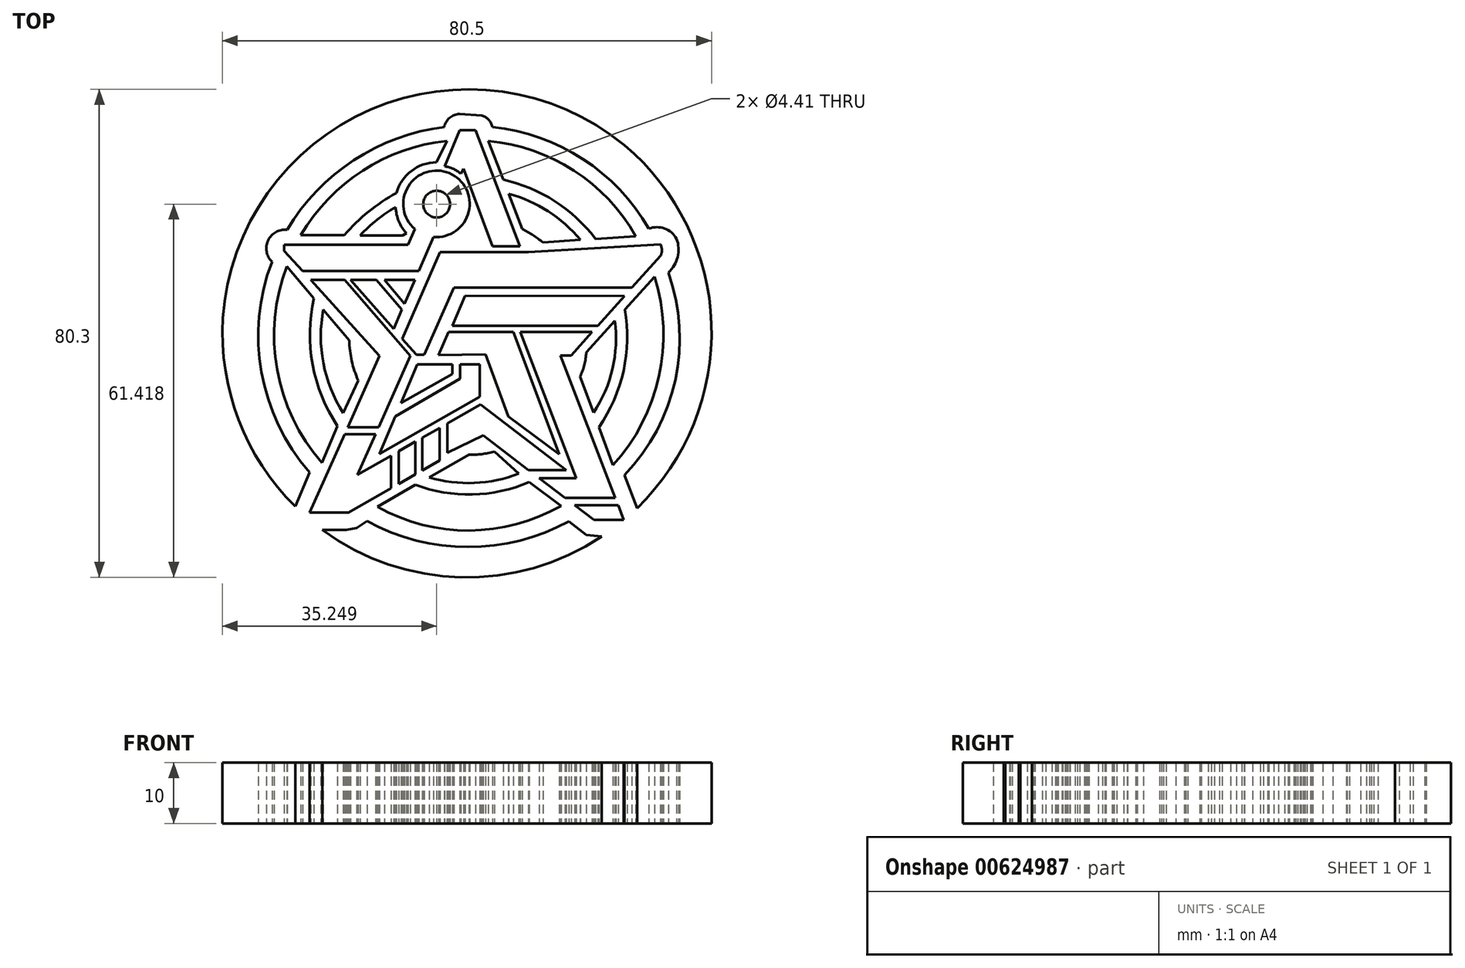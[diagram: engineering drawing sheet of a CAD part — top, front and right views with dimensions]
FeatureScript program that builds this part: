
annotation { "Feature Type Name" : "Feature", "Feature Type Description" : "" }
export const myFeature = defineFeature(function(context is Context, id is Id, definition is map)
    precondition{}
    {
        {
            var Q0;
            Q0=qCreatedBy(makeId("Top.planeOp"),FACE);
            var sketch = newSketch(context, id + "F0", { "sketchPlane" : qUnion([Q0])});
            skCircle(sketch, "E0", {"center": v(0, 0) * mm, "radius": 19.62 * mm, "construction": true});
            skCircle(sketch, "E1", {"center": v(0, 0) * mm, "radius": 24.24 * mm, "construction": true});
            skCircle(sketch, "E2", {"center": v(0, 0) * mm, "radius": 34.5 * mm, "construction": true});
            skLineSegment(sketch, "E3", {"start": v(20.7, -30.4) * mm, "end": v(2.49, -16.49) * mm, "construction": true});
            skLineSegment(sketch, "E4", {"start": v(2.49, -16.49) * mm, "end": v(-19.72, -29.2) * mm, "construction": true});
            skLineSegment(sketch, "E5", {"start": v(2, -11.38) * mm, "end": v(-18.24, -22.97) * mm, "construction": true});
            skLineSegment(sketch, "E6", {"start": v(-18.24, -22.97) * mm, "end": v(-9.56, -3.39) * mm, "construction": true});
            skLineSegment(sketch, "E7", {"start": v(-5.7, 16.2) * mm, "end": v(-12.28, 1.1) * mm, "construction": true});
            skLineSegment(sketch, "E8", {"start": v(-25.9, 9.11) * mm, "end": v(-8.79, 9.11) * mm, "construction": true});
            skLineSegment(sketch, "E9", {"start": v(23.83, -21.37) * mm, "end": v(18.4, -6.8) * mm, "construction": true});
            skLineSegment(sketch, "E10", {"start": v(30.66, 9.62) * mm, "end": v(19.42, -2.8) * mm, "construction": true});
            skLineSegment(sketch, "E11", {"start": v(25.58, -30.36) * mm, "end": v(15.19, -3.34) * mm, "construction": true});
            skLineSegment(sketch, "E12", {"start": v(15.19, -3.34) * mm, "end": v(16.91, -3.34) * mm, "construction": true});
            skLineSegment(sketch, "E13", {"start": v(16.91, -3.34) * mm, "end": v(31.66, 13.12) * mm, "construction": true});
            skLineSegment(sketch, "E14", {"start": v(27.56, 16.32) * mm, "end": v(12.3, 15.29) * mm, "construction": true});
            skLineSegment(sketch, "E15", {"start": v(3.31, 32) * mm, "end": v(8.9, 17.49) * mm, "construction": true});
            skArc(sketch, "E16", {"start": v(12.3, 15.29) * mm, "mid": v(10.66, 16.48) * mm, "end": v(8.9, 17.49) * mm});
            skArc(sketch, "E17", {"start": v(18.46, 15.7) * mm, "mid": v(13.15, 20.41) * mm, "end": v(6.66, 23.3) * mm});
            skArc(sketch, "E18", {"start": v(20.95, 15.87) * mm, "mid": v(14.22, 22.1) * mm, "end": v(5.77, 25.62) * mm});
            skArc(sketch, "E19", {"start": v(27.56, 16.32) * mm, "mid": v(17.36, 27.13) * mm, "end": v(3.31, 32) * mm});
            skLineSegment(sketch, "E20", {"start": v(3.31, 32) * mm, "end": v(5.77, 25.62) * mm});
            skLineSegment(sketch, "E21", {"start": v(6.66, 23.3) * mm, "end": v(8.9, 17.49) * mm});
            skLineSegment(sketch, "E22", {"start": v(12.3, 15.29) * mm, "end": v(18.46, 15.7) * mm});
            skLineSegment(sketch, "E23", {"start": v(20.95, 15.87) * mm, "end": v(27.56, 16.32) * mm});
            skLineSegment(sketch, "E24", {"start": v(-3.92, 27.8) * mm, "end": v(-1.42, 33.75) * mm});
            skLineSegment(sketch, "E25", {"start": v(-1.42, 33.75) * mm, "end": v(1.17, 33.75) * mm});
            skLineSegment(sketch, "E26", {"start": v(1.17, 33.75) * mm, "end": v(8.52, 14.66) * mm});
            skLineSegment(sketch, "E27", {"start": v(8.52, 14.66) * mm, "end": v(4.02, 14.66) * mm});
            skLineSegment(sketch, "E28", {"start": v(4.02, 14.66) * mm, "end": v(-0.78, 27.44) * mm});
            skLineSegment(sketch, "E29", {"start": v(-0.78, 27.44) * mm, "end": v(-1.24, 26.58) * mm});
            skArc(sketch, "E30", {"start": v(-1.24, 26.58) * mm, "mid": v(-2.48, 27.41) * mm, "end": v(-3.92, 27.8) * mm});
            skCircle(sketch, "E31", {"center": v(-5.21, 21.6) * mm, "radius": 2.2 * mm});
            skLineSegment(sketch, "E32", {"start": v(-5.7, 16.2) * mm, "end": v(-8.16, 10.56) * mm});
            skLineSegment(sketch, "E33", {"start": v(-8.16, 10.56) * mm, "end": v(-27.23, 10.56) * mm});
            skLineSegment(sketch, "E34", {"start": v(-27.23, 10.56) * mm, "end": v(-30.3, 13.9) * mm});
            skLineSegment(sketch, "E35", {"start": v(-30.3, 13.9) * mm, "end": v(-30.3, 14.9) * mm});
            skLineSegment(sketch, "E36", {"start": v(-30.3, 14.9) * mm, "end": v(-9.9, 14.9) * mm});
            skLineSegment(sketch, "E37", {"start": v(-9.9, 14.9) * mm, "end": v(-8.78, 17.49) * mm});
            skArc(sketch, "E38", {"start": v(-5.7, 16.2) * mm, "mid": v(-3.11, 26.69) * mm, "end": v(-8.78, 17.49) * mm});
            skLineSegment(sketch, "E39", {"start": v(-10.79, 16.46) * mm, "end": v(-10.16, 16.79) * mm});
            skLineSegment(sketch, "E40", {"start": v(-10.79, 16.46) * mm, "end": v(-17.8, 16.46) * mm});
            skArc(sketch, "E41", {"start": v(-11.95, 21.09) * mm, "mid": v(-15.04, 18.99) * mm, "end": v(-17.8, 16.46) * mm});
            skArc(sketch, "E42", {"start": v(-11.95, 21.09) * mm, "mid": v(-11.44, 18.78) * mm, "end": v(-10.16, 16.79) * mm});
            skArc(sketch, "E43", {"start": v(-5.2, 28.49) * mm, "mid": v(-9.36, 27.06) * mm, "end": v(-11.83, 23.42) * mm});
            skLineSegment(sketch, "E44", {"start": v(-5.2, 28.49) * mm, "end": v(-3.52, 32.02) * mm});
            skLineSegment(sketch, "E45", {"start": v(-20.38, 16.47) * mm, "end": v(-27.54, 16.47) * mm});
            skArc(sketch, "E46", {"start": v(-3.52, 32.02) * mm, "mid": v(-17.38, 27.1) * mm, "end": v(-27.54, 16.47) * mm});
            skArc(sketch, "E47", {"start": v(-11.83, 23.42) * mm, "mid": v(-16.43, 20.34) * mm, "end": v(-20.38, 16.47) * mm});
            skLineSegment(sketch, "E48", {"start": v(-13.82, 9.11) * mm, "end": v(-10.5, 5.18) * mm});
            skLineSegment(sketch, "E49", {"start": v(-10.5, 5.18) * mm, "end": v(-8.79, 9.11) * mm});
            skLineSegment(sketch, "E50", {"start": v(-13.82, 9.11) * mm, "end": v(-8.79, 9.11) * mm});
            skLineSegment(sketch, "E51", {"start": v(-19.38, 9.11) * mm, "end": v(-15.15, 9.11) * mm});
            skLineSegment(sketch, "E52", {"start": v(-15.15, 9.11) * mm, "end": v(-10.91, 4.22) * mm});
            skLineSegment(sketch, "E53", {"start": v(-10.91, 4.22) * mm, "end": v(-12.28, 1.1) * mm});
            skLineSegment(sketch, "E54", {"start": v(-12.28, 1.1) * mm, "end": v(-19.38, 9.11) * mm});
            skLineSegment(sketch, "E55", {"start": v(-25.9, 9.11) * mm, "end": v(-20.34, 9.11) * mm});
            skLineSegment(sketch, "E56", {"start": v(-20.34, 9.11) * mm, "end": v(-9.56, -3.39) * mm});
            skLineSegment(sketch, "E57", {"start": v(-9.56, -3.39) * mm, "end": v(-14.76, -15.11) * mm});
            skLineSegment(sketch, "E58", {"start": v(-14.76, -15.11) * mm, "end": v(-19.82, -15.11) * mm});
            skLineSegment(sketch, "E59", {"start": v(-19.82, -15.11) * mm, "end": v(-14.62, -3.39) * mm});
            skLineSegment(sketch, "E60", {"start": v(-14.62, -3.39) * mm, "end": v(-25.9, 9.11) * mm});
            skLineSegment(sketch, "E61", {"start": v(-7.25, -3.18) * mm, "end": v(-8.54, -3.18) * mm});
            skLineSegment(sketch, "E62", {"start": v(-8.54, -3.18) * mm, "end": v(-10.84, -0.58) * mm});
            skLineSegment(sketch, "E63", {"start": v(-10.84, -0.58) * mm, "end": v(-4.63, 13.7) * mm});
            skLineSegment(sketch, "E64", {"start": v(-4.63, 13.7) * mm, "end": v(9.88, 13.7) * mm});
            skLineSegment(sketch, "E65", {"start": v(9.88, 13.7) * mm, "end": v(31.6, 14.98) * mm});
            skLineSegment(sketch, "E66", {"start": v(31.66, 13.12) * mm, "end": v(26.93, 7.84) * mm});
            skLineSegment(sketch, "E67", {"start": v(26.93, 7.84) * mm, "end": v(-2.35, 7.84) * mm});
            skLineSegment(sketch, "E68", {"start": v(-2.35, 7.84) * mm, "end": v(-7.25, -3.18) * mm});
            skArc(sketch, "E69", {"start": v(31.66, 13.12) * mm, "mid": v(31.86, 14.06) * mm, "end": v(31.6, 14.98) * mm});
            skLineSegment(sketch, "E70", {"start": v(25.68, 6.44) * mm, "end": v(21.3, 1.56) * mm});
            skLineSegment(sketch, "E71", {"start": v(21.3, 1.56) * mm, "end": v(-2.63, 1.56) * mm});
            skLineSegment(sketch, "E72", {"start": v(-0.54, 6.55) * mm, "end": v(-4.93, -3.25) * mm, "construction": true});
            skLineSegment(sketch, "E73", {"start": v(1.9, -4.77) * mm, "end": v(-8.37, -4.77) * mm, "construction": true});
            skLineSegment(sketch, "E74", {"start": v(-8.37, -4.77) * mm, "end": v(-14.63, -19.5) * mm, "construction": true});
            skLineSegment(sketch, "E75", {"start": v(-11.07, -11.11) * mm, "end": v(-2.59, -6.39) * mm});
            skLineSegment(sketch, "E76", {"start": v(-2.59, -6.39) * mm, "end": v(-2.59, -4.77) * mm});
            skLineSegment(sketch, "E77", {"start": v(-2.59, -4.77) * mm, "end": v(-8.37, -4.77) * mm});
            skLineSegment(sketch, "E78", {"start": v(-11.07, -11.11) * mm, "end": v(-8.37, -4.77) * mm});
            skLineSegment(sketch, "E79", {"start": v(-1.37, -4.77) * mm, "end": v(1.9, -4.77) * mm});
            skLineSegment(sketch, "E80", {"start": v(1.9, -10.12) * mm, "end": v(1.9, -4.77) * mm});
            skLineSegment(sketch, "E81", {"start": v(1.9, -10.12) * mm, "end": v(-14.63, -19.5) * mm});
            skLineSegment(sketch, "E82", {"start": v(-1.37, -4.77) * mm, "end": v(-1.37, -7.1) * mm});
            skLineSegment(sketch, "E83", {"start": v(-1.37, -7.1) * mm, "end": v(-12.03, -13.38) * mm});
            skLineSegment(sketch, "E84", {"start": v(-12.03, -13.38) * mm, "end": v(-14.63, -19.5) * mm});
            skLineSegment(sketch, "E85", {"start": v(20.38, 0.53) * mm, "end": v(-3.24, 0.53) * mm, "construction": true});
            skLineSegment(sketch, "E86", {"start": v(-3.24, 0.53) * mm, "end": v(7.4, 0.53) * mm});
            skLineSegment(sketch, "E87", {"start": v(7.4, 0.53) * mm, "end": v(14.97, -19.6) * mm});
            skLineSegment(sketch, "E88", {"start": v(14.97, -19.6) * mm, "end": v(6.62, -13.36) * mm});
            skLineSegment(sketch, "E89", {"start": v(6.62, -13.36) * mm, "end": v(2.87, -3.12) * mm});
            skLineSegment(sketch, "E90", {"start": v(2.87, -3.12) * mm, "end": v(-4.93, -3.25) * mm});
            skLineSegment(sketch, "E91", {"start": v(-4.93, -3.25) * mm, "end": v(-3.24, 0.53) * mm});
            skLineSegment(sketch, "E92", {"start": v(20.38, 0.53) * mm, "end": v(8.57, 0.53) * mm});
            skLineSegment(sketch, "E93", {"start": v(8.57, 0.53) * mm, "end": v(17.74, -23.52) * mm});
            skLineSegment(sketch, "E94", {"start": v(17.74, -23.52) * mm, "end": v(11.7, -23.52) * mm});
            skLineSegment(sketch, "E95", {"start": v(11.7, -23.52) * mm, "end": v(15.95, -26.77) * mm});
            skLineSegment(sketch, "E96", {"start": v(15.95, -26.77) * mm, "end": v(24.2, -26.77) * mm});
            skLineSegment(sketch, "E97", {"start": v(24.2, -26.77) * mm, "end": v(15.19, -3.34) * mm});
            skLineSegment(sketch, "E98", {"start": v(15.19, -3.34) * mm, "end": v(16.91, -3.34) * mm});
            skLineSegment(sketch, "E99", {"start": v(16.91, -3.34) * mm, "end": v(20.38, 0.53) * mm});
            skLineSegment(sketch, "E100", {"start": v(-2.63, 1.56) * mm, "end": v(-0.54, 6.55) * mm});
            skLineSegment(sketch, "E101", {"start": v(-0.54, 6.55) * mm, "end": v(25.68, 6.44) * mm});
            skArc(sketch, "E102", {"start": v(18.4, -6.8) * mm, "mid": v(19.1, -4.85) * mm, "end": v(19.42, -2.8) * mm});
            skArc(sketch, "E103", {"start": v(20.62, -12.74) * mm, "mid": v(23.74, -5.5) * mm, "end": v(24.12, 2.38) * mm});
            skArc(sketch, "E104", {"start": v(21.5, -15.12) * mm, "mid": v(25.55, -5.86) * mm, "end": v(25.8, 4.24) * mm});
            skArc(sketch, "E105", {"start": v(23.83, -21.37) * mm, "mid": v(31.37, -6.79) * mm, "end": v(30.66, 9.62) * mm});
            skLineSegment(sketch, "E106", {"start": v(30.66, 9.62) * mm, "end": v(25.8, 4.24) * mm});
            skLineSegment(sketch, "E107", {"start": v(24.12, 2.38) * mm, "end": v(19.42, -2.8) * mm});
            skLineSegment(sketch, "E108", {"start": v(18.4, -6.8) * mm, "end": v(20.62, -12.74) * mm});
            skLineSegment(sketch, "E109", {"start": v(21.5, -15.12) * mm, "end": v(23.83, -21.37) * mm});
            skLineSegment(sketch, "E110", {"start": v(17.52, -27.97) * mm, "end": v(24.66, -27.97) * mm});
            skLineSegment(sketch, "E111", {"start": v(24.66, -27.97) * mm, "end": v(25.58, -30.36) * mm});
            skLineSegment(sketch, "E112", {"start": v(25.58, -30.36) * mm, "end": v(20.7, -30.4) * mm});
            skLineSegment(sketch, "E113", {"start": v(20.7, -30.4) * mm, "end": v(17.52, -27.97) * mm});
            skArc(sketch, "E114", {"start": v(0, -19.62) * mm, "mid": v(2.16, -19.55) * mm, "end": v(4.29, -19.15) * mm});
            skArc(sketch, "E115", {"start": v(-6.43, -23.37) * mm, "mid": v(1, -24.3) * mm, "end": v(8.3, -22.77) * mm});
            skArc(sketch, "E116", {"start": v(-8.72, -24.58) * mm, "mid": v(0.68, -26.2) * mm, "end": v(10, -24.17) * mm});
            skArc(sketch, "E117", {"start": v(-14.96, -28.23) * mm, "mid": v(0.19, -32.12) * mm, "end": v(15.28, -28.06) * mm});
            skLineSegment(sketch, "E118", {"start": v(15.28, -28.06) * mm, "end": v(10, -24.17) * mm});
            skLineSegment(sketch, "E119", {"start": v(8.3, -22.77) * mm, "end": v(4.29, -19.15) * mm});
            skLineSegment(sketch, "E120", {"start": v(-6.43, -23.37) * mm, "end": v(0.1, -19.62) * mm});
            skLineSegment(sketch, "E121", {"start": v(-8.72, -24.58) * mm, "end": v(-14.96, -28.23) * mm});
            skLineSegment(sketch, "E122", {"start": v(-3.41, -19.32) * mm, "end": v(-3.41, -14.49) * mm});
            skLineSegment(sketch, "E123", {"start": v(-3.41, -14.49) * mm, "end": v(2, -11.38) * mm});
            skLineSegment(sketch, "E124", {"start": v(2, -11.38) * mm, "end": v(16.13, -22.15) * mm});
            skLineSegment(sketch, "E125", {"start": v(16.13, -22.15) * mm, "end": v(9.9, -22.15) * mm});
            skLineSegment(sketch, "E126", {"start": v(9.9, -22.15) * mm, "end": v(2.49, -16.49) * mm});
            skLineSegment(sketch, "E127", {"start": v(2.49, -16.49) * mm, "end": v(-3.41, -19.32) * mm});
            skLineSegment(sketch, "E128", {"start": v(-4.73, -15.24) * mm, "end": v(-4.73, -20.62) * mm});
            skLineSegment(sketch, "E129", {"start": v(-4.73, -20.62) * mm, "end": v(-7.57, -22.25) * mm});
            skLineSegment(sketch, "E130", {"start": v(-7.57, -22.25) * mm, "end": v(-7.57, -16.87) * mm});
            skLineSegment(sketch, "E131", {"start": v(-7.57, -16.87) * mm, "end": v(-4.73, -15.24) * mm});
            skLineSegment(sketch, "E132", {"start": v(-8.7, -17.5) * mm, "end": v(-8.7, -22.89) * mm});
            skLineSegment(sketch, "E133", {"start": v(-8.7, -22.89) * mm, "end": v(-11.42, -24.45) * mm});
            skLineSegment(sketch, "E134", {"start": v(-11.42, -24.45) * mm, "end": v(-11.42, -19.07) * mm});
            skLineSegment(sketch, "E135", {"start": v(-11.42, -19.07) * mm, "end": v(-8.7, -17.5) * mm});
            skLineSegment(sketch, "E136", {"start": v(-12.7, -19.8) * mm, "end": v(-12.7, -25.18) * mm});
            skLineSegment(sketch, "E137", {"start": v(-12.7, -25.18) * mm, "end": v(-19.72, -29.2) * mm});
            skLineSegment(sketch, "E138", {"start": v(-26.12, -29.2) * mm, "end": v(-20.34, -16.27) * mm});
            skLineSegment(sketch, "E139", {"start": v(-20.34, -16.27) * mm, "end": v(-15.27, -16.27) * mm});
            skLineSegment(sketch, "E140", {"start": v(-15.27, -16.27) * mm, "end": v(-18.24, -22.97) * mm});
            skLineSegment(sketch, "E141", {"start": v(-18.24, -22.97) * mm, "end": v(-12.7, -19.8) * mm});
            skLineSegment(sketch, "E142", {"start": v(-18.24, -7.23) * mm, "end": v(-24.08, -20.94) * mm, "construction": true});
            skLineSegment(sketch, "E143", {"start": v(-19.57, -0.83) * mm, "end": v(-29.85, 11.36) * mm, "construction": true});
            skArc(sketch, "E144", {"start": v(-19.57, -0.83) * mm, "mid": v(-19.18, -4.21) * mm, "end": v(-18.1, -7.44) * mm});
            skArc(sketch, "E145", {"start": v(-23.86, 4.26) * mm, "mid": v(-23.85, -4.56) * mm, "end": v(-20.6, -12.77) * mm});
            skArc(sketch, "E146", {"start": v(-25.4, 6.09) * mm, "mid": v(-25.63, -4.81) * mm, "end": v(-21.51, -14.9) * mm});
            skArc(sketch, "E147", {"start": v(-29.85, 11.36) * mm, "mid": v(-31.47, -5.6) * mm, "end": v(-24.08, -20.94) * mm});
            skLineSegment(sketch, "E148", {"start": v(-19.57, -0.83) * mm, "end": v(-23.86, 4.26) * mm});
            skLineSegment(sketch, "E149", {"start": v(-25.4, 6.09) * mm, "end": v(-29.85, 11.36) * mm});
            skLineSegment(sketch, "E150", {"start": v(-18.1, -7.44) * mm, "end": v(-20.6, -12.77) * mm});
            skLineSegment(sketch, "E151", {"start": v(-21.51, -14.9) * mm, "end": v(-24.08, -20.94) * mm});
            skPoint(sketch, "E152.endSnap0", {"position": v(-25.63, -4.81) * mm});
            skArc(sketch, "E153", {"start": v(25.72, -23) * mm, "mid": v(34.06, -7.35) * mm, "end": v(32.92, 10.35) * mm});
            skArc(sketch, "E154", {"start": v(29.71, 17.55) * mm, "mid": v(18.86, 29.01) * mm, "end": v(3.98, 34.28) * mm});
            skArc(sketch, "E155", {"start": v(-3.98, 34.28) * mm, "mid": v(-18.86, 28.81) * mm, "end": v(-29.82, 17.37) * mm});
            skArc(sketch, "E156", {"start": v(-29.82, 17.37) * mm, "mid": v(-32.94, 15.64) * mm, "end": v(-32.3, 12.14) * mm});
            skArc(sketch, "E157", {"start": v(-1.42, 36.44) * mm, "mid": v(-3.07, 35.8) * mm, "end": v(-3.98, 34.28) * mm});
            skArc(sketch, "E158", {"start": v(3.98, 34.28) * mm, "mid": v(3.36, 35.48) * mm, "end": v(2.22, 36.2) * mm});
            skLineSegment(sketch, "E159", {"start": v(2.22, 36.2) * mm, "end": v(-1.42, 36.44) * mm});
            skArc(sketch, "E160", {"start": v(34.3, 15.87) * mm, "mid": v(32.32, 17.57) * mm, "end": v(29.71, 17.55) * mm});
            skArc(sketch, "E161", {"start": v(32.92, 10.35) * mm, "mid": v(34.45, 12.9) * mm, "end": v(34.3, 15.87) * mm});
            skLineSegment(sketch, "E162", {"start": v(25.72, -23) * mm, "end": v(27.79, -28.43) * mm});
            skLineSegment(sketch, "E163", {"start": v(19.4, -32.85) * mm, "end": v(21.95, -33.13) * mm});
            skLineSegment(sketch, "E164", {"start": v(-18.36, -31.69) * mm, "end": v(-20.07, -32.03) * mm});
            skLineSegment(sketch, "E165", {"start": v(-20.07, -32.03) * mm, "end": v(-24.02, -32.03) * mm});
            skArc(sketch, "E166", {"start": v(-32.3, 12.14) * mm, "mid": v(-34.03, -6.06) * mm, "end": v(-26.13, -22.54) * mm});
            skLineSegment(sketch, "E167", {"start": v(-26.13, -22.54) * mm, "end": v(-28.48, -28.16) * mm});
            skArc(sketch, "E168", {"start": v(27.79, -28.43) * mm, "mid": v(0, 40.74) * mm, "end": v(-28.48, -28.16) * mm});
            skArc(sketch, "E169", {"start": v(-16.63, -30.59) * mm, "mid": v(-0.02, -34.84) * mm, "end": v(16.59, -30.6) * mm});
            skLineSegment(sketch, "E170", {"start": v(19.4, -32.85) * mm, "end": v(16.59, -30.6) * mm});
            skLineSegment(sketch, "E171", {"start": v(-18.36, -31.69) * mm, "end": v(-16.63, -30.59) * mm});
            skArc(sketch, "E172", {"start": v(-24.02, -32.03) * mm, "mid": v(-1.2, -39.8) * mm, "end": v(21.95, -33.13) * mm});
            skCircle(sketch, "E173", {"center": v(0.01, -0.03) * mm, "radius": 40.5 * mm});
            skCircle(sketch, "E174", {"center": v(0.01, -0.03) * mm, "radius": 41.57 * mm});
            skLineSegment(sketch, "E175", {"start": v(-19.72, -29.2) * mm, "end": v(-26.12, -29.2) * mm});
            skSolve(sketch);
        }
        {
            var Q0;
            Q0=makeQuery(id+"F0.imprint","IMPRINT",FACE,{"disambiguationData":[TD([[makeQuery(id+"F0.imprint","IMPRINT",EDGE,{"derivedFrom":sQuery(id+"F0.wireOp",EDGE,"E31")}),-1.0]])]});
            var Q1;
            Q1=makeQuery(id+"F0.imprint","IMPRINT",FACE,{"disambiguationData":[TD([[makeQuery(id+"F0.imprint","IMPRINT",EDGE,{"derivedFrom":sQuery(id+"F0.wireOp",EDGE,"E39")}),1.0]])]});
            var Q2;
            Q2=makeQuery(id+"F0.imprint","IMPRINT",FACE,{"disambiguationData":[TD([[makeQuery(id+"F0.imprint","IMPRINT",EDGE,{"derivedFrom":sQuery(id+"F0.wireOp",EDGE,"E43")}),-1.0]])]});
            var Q3;
            Q3=makeQuery(id+"F0.imprint","IMPRINT",FACE,{"disambiguationData":[TD([[makeQuery(id+"F0.imprint","IMPRINT",EDGE,{"derivedFrom":sQuery(id+"F0.wireOp",EDGE,"E24")}),-1.0]])]});
            var Q4;
            Q4=makeQuery(id+"F0.imprint","IMPRINT",FACE,{"disambiguationData":[TD([[makeQuery(id+"F0.imprint","IMPRINT",EDGE,{"derivedFrom":sQuery(id+"F0.wireOp",EDGE,"E18")}),-1.0]])]});
            var Q5;
            Q5=makeQuery(id+"F0.imprint","IMPRINT",FACE,{"disambiguationData":[TD([[makeQuery(id+"F0.imprint","IMPRINT",EDGE,{"derivedFrom":sQuery(id+"F0.wireOp",EDGE,"E16")}),-1.0]])]});
            var Q6;
            Q6=makeQuery(id+"F0.imprint","IMPRINT",FACE,{"disambiguationData":[TD([[makeQuery(id+"F0.imprint","IMPRINT",EDGE,{"derivedFrom":sQuery(id+"F0.wireOp",EDGE,"E61")}),-1.0]])]});
            var Q7;
            Q7=makeQuery(id+"F0.imprint","IMPRINT",FACE,{"disambiguationData":[TD([[makeQuery(id+"F0.imprint","IMPRINT",EDGE,{"derivedFrom":sQuery(id+"F0.wireOp",EDGE,"E70")}),-1.0]])]});
            var Q8;
            Q8=makeQuery(id+"F0.imprint","IMPRINT",FACE,{"disambiguationData":[TD([[makeQuery(id+"F0.imprint","IMPRINT",EDGE,{"derivedFrom":sQuery(id+"F0.wireOp",EDGE,"E48")}),1.0]])]});
            var Q9;
            Q9=makeQuery(id+"F0.imprint","IMPRINT",FACE,{"disambiguationData":[TD([[makeQuery(id+"F0.imprint","IMPRINT",EDGE,{"derivedFrom":sQuery(id+"F0.wireOp",EDGE,"E51")}),-1.0]])]});
            var Q10;
            Q10=makeQuery(id+"F0.imprint","IMPRINT",FACE,{"disambiguationData":[TD([[makeQuery(id+"F0.imprint","IMPRINT",EDGE,{"derivedFrom":sQuery(id+"F0.wireOp",EDGE,"E55")}),-1.0]])]});
            var Q11;
            Q11=makeQuery(id+"F0.imprint","IMPRINT",FACE,{"disambiguationData":[TD([[makeQuery(id+"F0.imprint","IMPRINT",EDGE,{"derivedFrom":sQuery(id+"F0.wireOp",EDGE,"E75")}),1.0]])]});
            var Q12;
            Q12=makeQuery(id+"F0.imprint","IMPRINT",FACE,{"disambiguationData":[TD([[makeQuery(id+"F0.imprint","IMPRINT",EDGE,{"derivedFrom":sQuery(id+"F0.wireOp",EDGE,"E79")}),-1.0]])]});
            var Q13;
            Q13=makeQuery(id+"F0.imprint","IMPRINT",FACE,{"disambiguationData":[TD([[makeQuery(id+"F0.imprint","IMPRINT",EDGE,{"derivedFrom":sQuery(id+"F0.wireOp",EDGE,"E86")}),-1.0]])]});
            var Q14;
            Q14=makeQuery(id+"F0.imprint","IMPRINT",FACE,{"disambiguationData":[TD([[makeQuery(id+"F0.imprint","IMPRINT",EDGE,{"derivedFrom":sQuery(id+"F0.wireOp",EDGE,"E92")}),1.0]])]});
            var Q15;
            Q15=makeQuery(id+"F0.imprint","IMPRINT",FACE,{"disambiguationData":[TD([[makeQuery(id+"F0.imprint","IMPRINT",EDGE,{"derivedFrom":sQuery(id+"F0.wireOp",EDGE,"E102")}),-1.0]])]});
            var Q16;
            Q16=makeQuery(id+"F0.imprint","IMPRINT",FACE,{"disambiguationData":[TD([[makeQuery(id+"F0.imprint","IMPRINT",EDGE,{"derivedFrom":sQuery(id+"F0.wireOp",EDGE,"E104")}),-1.0]])]});
            var Q17;
            Q17=makeQuery(id+"F0.imprint","IMPRINT",FACE,{"disambiguationData":[TD([[makeQuery(id+"F0.imprint","IMPRINT",EDGE,{"derivedFrom":sQuery(id+"F0.wireOp",EDGE,"E153")}),-1.0]])]});
            var Q18;
            Q18=makeQuery(id+"F0.imprint","IMPRINT",FACE,{"disambiguationData":[TD([[makeQuery(id+"F0.imprint","IMPRINT",EDGE,{"derivedFrom":sQuery(id+"F0.wireOp",EDGE,"E110")}),-1.0]])]});
            var Q19;
            Q19=makeQuery(id+"F0.imprint","IMPRINT",FACE,{"disambiguationData":[TD([[makeQuery(id+"F0.imprint","IMPRINT",EDGE,{"derivedFrom":sQuery(id+"F0.wireOp",EDGE,"E116")}),-1.0]])]});
            var Q20;
            Q20=makeQuery(id+"F0.imprint","IMPRINT",FACE,{"disambiguationData":[TD([[makeQuery(id+"F0.imprint","IMPRINT",EDGE,{"derivedFrom":sQuery(id+"F0.wireOp",EDGE,"E163")}),-1.0]])]});
            var Q21;
            {var subQ4=sQuery(id+"F0.wireOp",EDGE,"E115");Q21=makeQuery(id+"F0.imprint","IMPRINT",FACE,{"disambiguationData":[TD([[makeQuery(id+"F0.imprint","IMPRINT",EDGE,{"derivedFrom":subQ4}),1.0]])]});}
            var Q22;
            Q22=makeQuery(id+"F0.imprint","IMPRINT",FACE,{"disambiguationData":[TD([[makeQuery(id+"F0.imprint","IMPRINT",EDGE,{"derivedFrom":sQuery(id+"F0.wireOp",EDGE,"E122")}),-1.0]])]});
            var Q23;
            Q23=makeQuery(id+"F0.imprint","IMPRINT",FACE,{"disambiguationData":[TD([[makeQuery(id+"F0.imprint","IMPRINT",EDGE,{"derivedFrom":sQuery(id+"F0.wireOp",EDGE,"E128")}),-1.0]])]});
            var Q24;
            Q24=makeQuery(id+"F0.imprint","IMPRINT",FACE,{"disambiguationData":[TD([[makeQuery(id+"F0.imprint","IMPRINT",EDGE,{"derivedFrom":sQuery(id+"F0.wireOp",EDGE,"E132")}),-1.0]])]});
            var Q25;
            Q25=makeQuery(id+"F0.imprint","IMPRINT",FACE,{"disambiguationData":[TD([[makeQuery(id+"F0.imprint","IMPRINT",EDGE,{"derivedFrom":sQuery(id+"F0.wireOp",EDGE,"E144")}),-1.0]])]});
            var Q26;
            Q26=makeQuery(id+"F0.imprint","IMPRINT",FACE,{"disambiguationData":[TD([[makeQuery(id+"F0.imprint","IMPRINT",EDGE,{"derivedFrom":sQuery(id+"F0.wireOp",EDGE,"E146")}),-1.0]])]});
            var Q27;
            Q27=makeQuery(id+"F0.imprint","IMPRINT",FACE,{"disambiguationData":[TD([[makeQuery(id+"F0.imprint","IMPRINT",EDGE,{"derivedFrom":sQuery(id+"F0.wireOp",EDGE,"E136")}),-1.0]])]});
            extrude(context, id + "F1", {"entities" : qUnion([Q0, Q1, Q2, Q3, Q4, Q5, Q6, Q7, Q8, Q9, Q10, Q11, Q12, Q13, Q14, Q15, Q16, Q17, Q18, Q19, Q20, Q21, Q22, Q23, Q24, Q25, Q26, Q27]), "depth" : 10 * mm, "offsetDistance" : 25 * mm});
        }
    });
